# Revit family: СМ-ВО_Eng
name_source: partatom
category: Duct Accessories
units: mm (PartAtom-declared; Revit-internal decimal feet)

## family parameters
Always vertical = Yes
Cut with Voids When Loaded = No
Part Type = Attaches To
Round Connector Dimension = Use Diameter
Shared = No
Work Plane-Based = No

## types (8) — shared parameters
00_20_Manufacturer = Vents
00_20_Name = Mounting curb
Casing Material = Metal, painted, blue, matte RAL 5007
Height = 550 mm
Load Classification = HVAC
Maintenance zone material = <By Category>
Manufacturer = Vents
URL = https://ventilation-system.com
zero-valued in all types: Default Elevation

## per-type parameters (varying)
| type | A | B | C | Corner | D | Dy | Length | Weight | Width | Фаска |
| SM-VO-0010-315/355 | 480 mm  [stored 1.5748 ft] | 590 mm  [stored 1.9357 ft] | 800 mm  [stored 2.62467 ft] | 400 mm  [stored 1.31234 ft] | 505 mm  [stored 1.65682 ft] | 500 mm  [stored 1.64042 ft] | 800 mm  [stored 2.62467 ft] | 43.50 kg | 800 mm  [stored 2.62467 ft] | 126 mm |
| SM-VO-0010-400/450 | 580 mm  [stored 1.90289 ft] | 692 mm  [stored 2.27034 ft] | 900 mm  [stored 2.95276 ft] | 500 mm  [stored 1.64042 ft] | 605 mm  [stored 1.98491 ft] | 600 mm | 900 mm  [stored 2.95276 ft] | 51.50 kg | 900 mm  [stored 2.95276 ft] | 151 mm  [stored 0.495407 ft] |
| SM-VO-0010-500 | 640 mm  [stored 2.09974 ft] | 760 mm | 970 mm  [stored 3.18241 ft] | 570 mm  [stored 1.87008 ft] | 675 mm  [stored 2.21457 ft] | 670 mm  [stored 2.19816 ft] | 970 mm  [stored 3.18241 ft] | 56.00 kg | 970 mm  [stored 3.18241 ft] | 169 mm |
| SM-VO-0010-560/630 | 750 mm  [stored 2.46063 ft] | 910 mm | 1120 mm  [stored 3.67454 ft] | 730 mm  [stored 2.39501 ft] | 835 mm | 830 mm  [stored 2.7231 ft] | 1120 mm  [stored 3.67454 ft] | 66.50 kg | 1120 mm  [stored 3.67454 ft] | 209 mm |
| SM-VO-0010-710/800 | 980 mm  [stored 3.21522 ft] | 1140 mm | 1350 mm | 950 mm  [stored 3.1168 ft] | 1055 mm  [stored 3.46129 ft] | 1050 mm  [stored 3.44488 ft] | 1350 mm | 83.00 kg | 1350 mm | 264 mm |
| SM-VO-0010-900 | 1050 mm  [stored 3.44488 ft] | 1208 mm | 1420 mm | 1000 mm  [stored 3.28084 ft] | 1105 mm  [stored 3.62533 ft] | 1100 mm  [stored 3.60892 ft] | 1420 mm | 88.50 kg | 1420 mm | 276 mm |
| SM-VO-0010-1000/1120 | 1340 mm | 1498 mm | 1710 mm | 1300 mm | 1405 mm | 1400 mm | 1710 mm | 112.00 kg | 1710 mm | 351 mm |
| SM-VO-0010-1250 | 1500 mm | 1688 mm | 1900 mm | 1500 mm | 1605 mm | 1600 mm | 1900 mm | 151.00 kg | 1900 mm | 401 mm |

note: column(s) folded — value = type name in every type: 00_20_Type

note: [stored X ft] marks values corroborated as IEEE doubles in the binary element streams (Revit-internal decimal feet)
